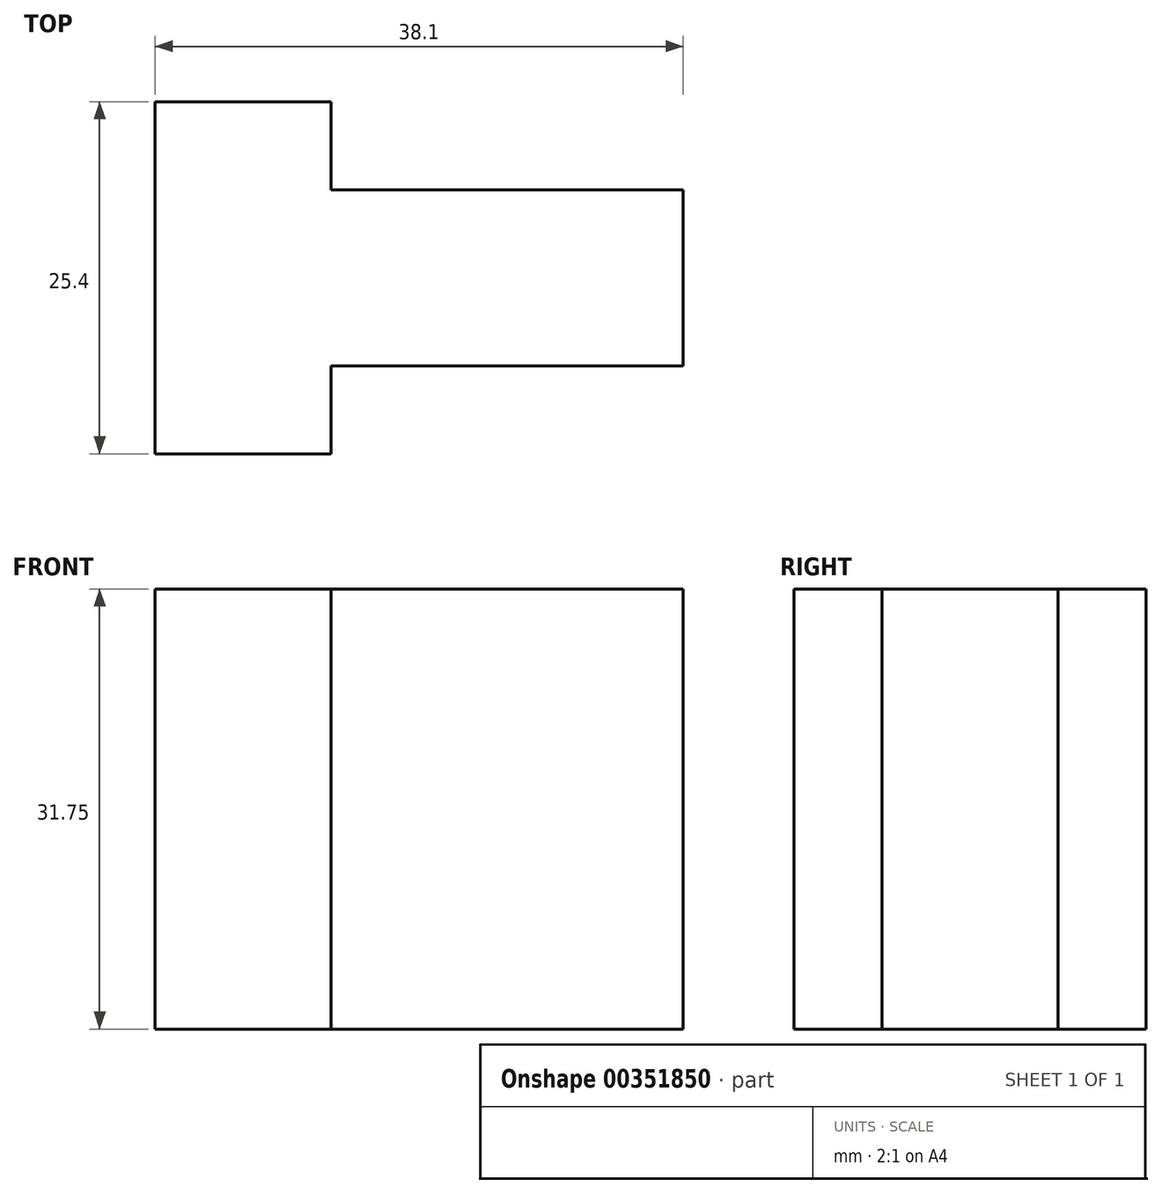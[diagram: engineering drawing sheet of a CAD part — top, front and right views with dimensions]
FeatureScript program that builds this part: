
annotation { "Feature Type Name" : "Feature", "Feature Type Description" : "" }
export const myFeature = defineFeature(function(context is Context, id is Id, definition is map)
    precondition{}
    {
        {
            var Q0;
            Q0=qCreatedBy(makeId("Top.planeOp"),FACE);
            var sketch = newSketch(context, id + "F0", { "sketchPlane" : qUnion([Q0])});
            skLineSegment(sketch, "E0", {"start": v(0, 0) * mm, "end": v(0, 25.4) * mm});
            skLineSegment(sketch, "E1", {"start": v(0, 25.4) * mm, "end": v(12.7, 25.4) * mm});
            skLineSegment(sketch, "E2", {"start": v(12.7, 25.4) * mm, "end": v(12.7, 19.05) * mm});
            skLineSegment(sketch, "E3", {"start": v(12.7, 19.05) * mm, "end": v(38.1, 19.05) * mm});
            skLineSegment(sketch, "E4", {"start": v(38.1, 19.05) * mm, "end": v(38.1, 6.35) * mm});
            skLineSegment(sketch, "E5", {"start": v(38.1, 6.35) * mm, "end": v(12.7, 6.35) * mm});
            skLineSegment(sketch, "E6", {"start": v(12.7, 6.35) * mm, "end": v(12.7, 0) * mm});
            skLineSegment(sketch, "E7", {"start": v(12.7, 0) * mm, "end": v(0, 0) * mm});
            skSolve(sketch);
        }
        {
            var Q0;
            Q0=makeQuery(id+"F0.imprint","IMPRINT",FACE,{"disambiguationData":[TD([[makeQuery(id+"F0.imprint","IMPRINT",EDGE,{"derivedFrom":sQuery(id+"F0.wireOp",EDGE,"E0")}),-1.0]])]});
            extrude(context, id + "F1", {"entities" : qUnion([Q0]), "depth" : 31.75 * mm});
        }
    });
